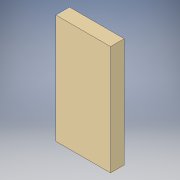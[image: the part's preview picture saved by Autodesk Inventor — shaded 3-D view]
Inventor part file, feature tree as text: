
AUTODESK INVENTOR PART (.ipt)
format: ipt  version: 2019 (Build 230136000, 136)  size: 92,672 bytes
history: native  units: in
note: dims shown in document units (in); Inventor stores cm internally (conversion verified against a paired STEP export)
features: extrude x1, sketch x1
ambient origin geometry x8: Origin, YZ Plane, XZ Plane, XY Plane, X Axis, Y Axis, Z Axis, Center Point
bodies: Solid1 (feature_tree)
feature tree (2):
  extrude  "Extrusion1"  Depth=1.0in
  sketch  "Sketch1"  dims[d0=0.5in d1=1.0in d2=0.125in d3=0.0in]
